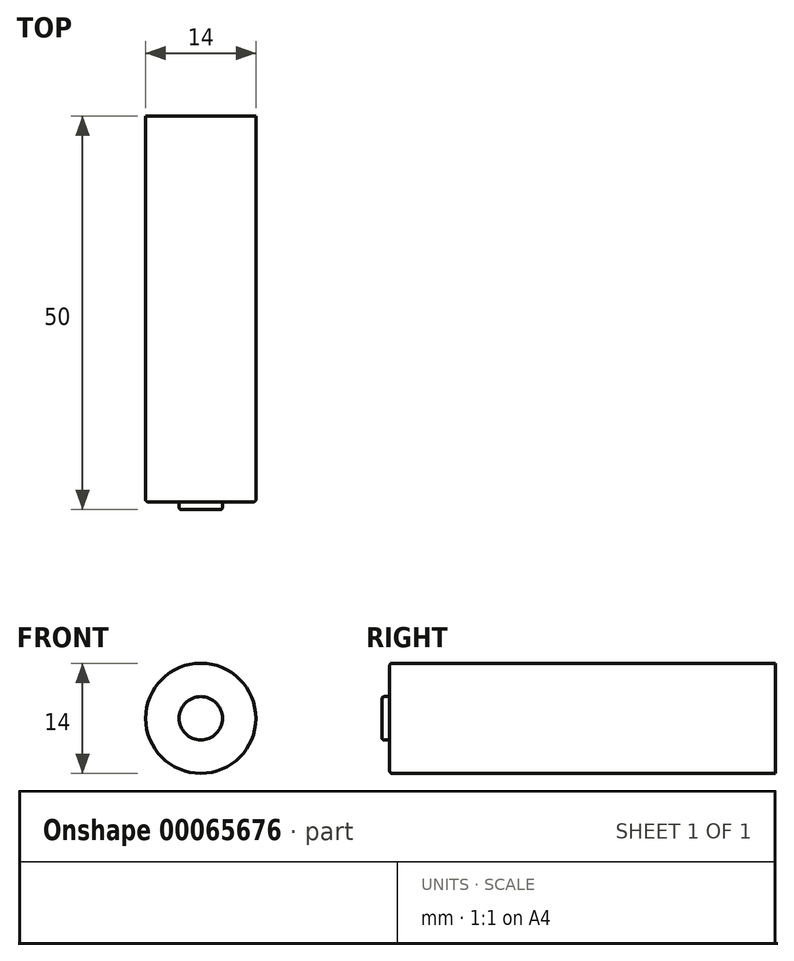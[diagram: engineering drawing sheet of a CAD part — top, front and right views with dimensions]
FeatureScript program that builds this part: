
annotation { "Feature Type Name" : "Feature", "Feature Type Description" : "" }
export const myFeature = defineFeature(function(context is Context, id is Id, definition is map)
    precondition{}
    {
        {
            var Q0;
            Q0=qCreatedBy(makeId("Front.planeOp"),FACE);
            var sketch = newSketch(context, id + "F0", { "sketchPlane" : qUnion([Q0])});
            skCircle(sketch, "E0", {"center": v(0, 0) * mm, "radius": 7 * mm});
            skCircle(sketch, "E1", {"center": v(0, 0) * mm, "radius": 2.75 * mm});
            skSolve(sketch);
        }
        {
            var Q0;
            Q0=makeQuery(id+"F0.imprint","IMPRINT",FACE,{"disambiguationData":[TD([[makeQuery(id+"F0.imprint","IMPRINT",EDGE,{"derivedFrom":sQuery(id+"F0.wireOp",EDGE,"E1")}),1.0]])]});
            var Q1;
            Q1=makeQuery(id+"F0.imprint","IMPRINT",FACE,{"disambiguationData":[TD([[makeQuery(id+"F0.imprint","IMPRINT",EDGE,{"derivedFrom":sQuery(id+"F0.wireOp",EDGE,"E0")}),1.0]])]});
            extrude(context, id + "F1", {"entities" : qUnion([Q0, Q1]), "oppositeDirection" : true, "depth" : 49 * mm});
        }
        {
            var Q0;
            Q0=makeQuery(id+"F0.imprint","IMPRINT",FACE,{"disambiguationData":[TD([[makeQuery(id+"F0.imprint","IMPRINT",EDGE,{"derivedFrom":sQuery(id+"F0.wireOp",EDGE,"E1")}),1.0]])]});
            extrude(context, id + "F2", {"entities" : qUnion([Q0]), "operationType" : NewBodyOperationType.ADD, "depth" : 1 * mm});
        }
        {
            var Q0;
            Q0=makeQuery(id+"F2.opExtrude","CAP_EDGE",EDGE,{"disambiguationData":[OSD([sQuery(id+"F0.wireOp",EDGE,"E1")])],"isStart":false});
            var Q1;
            Q1=makeQuery(id+"F1.opExtrude","CAP_EDGE",EDGE,{"disambiguationData":[OSD([sQuery(id+"F0.wireOp",EDGE,"E0")])],"isStart":true});
            fillet(context, id + "F3", {"entities" : qUnion([Q0, Q1]), "radius" : 0.3 * mm, "tangentPropagation" : true, "allowEdgeOverflow" : false});
        }
    });
